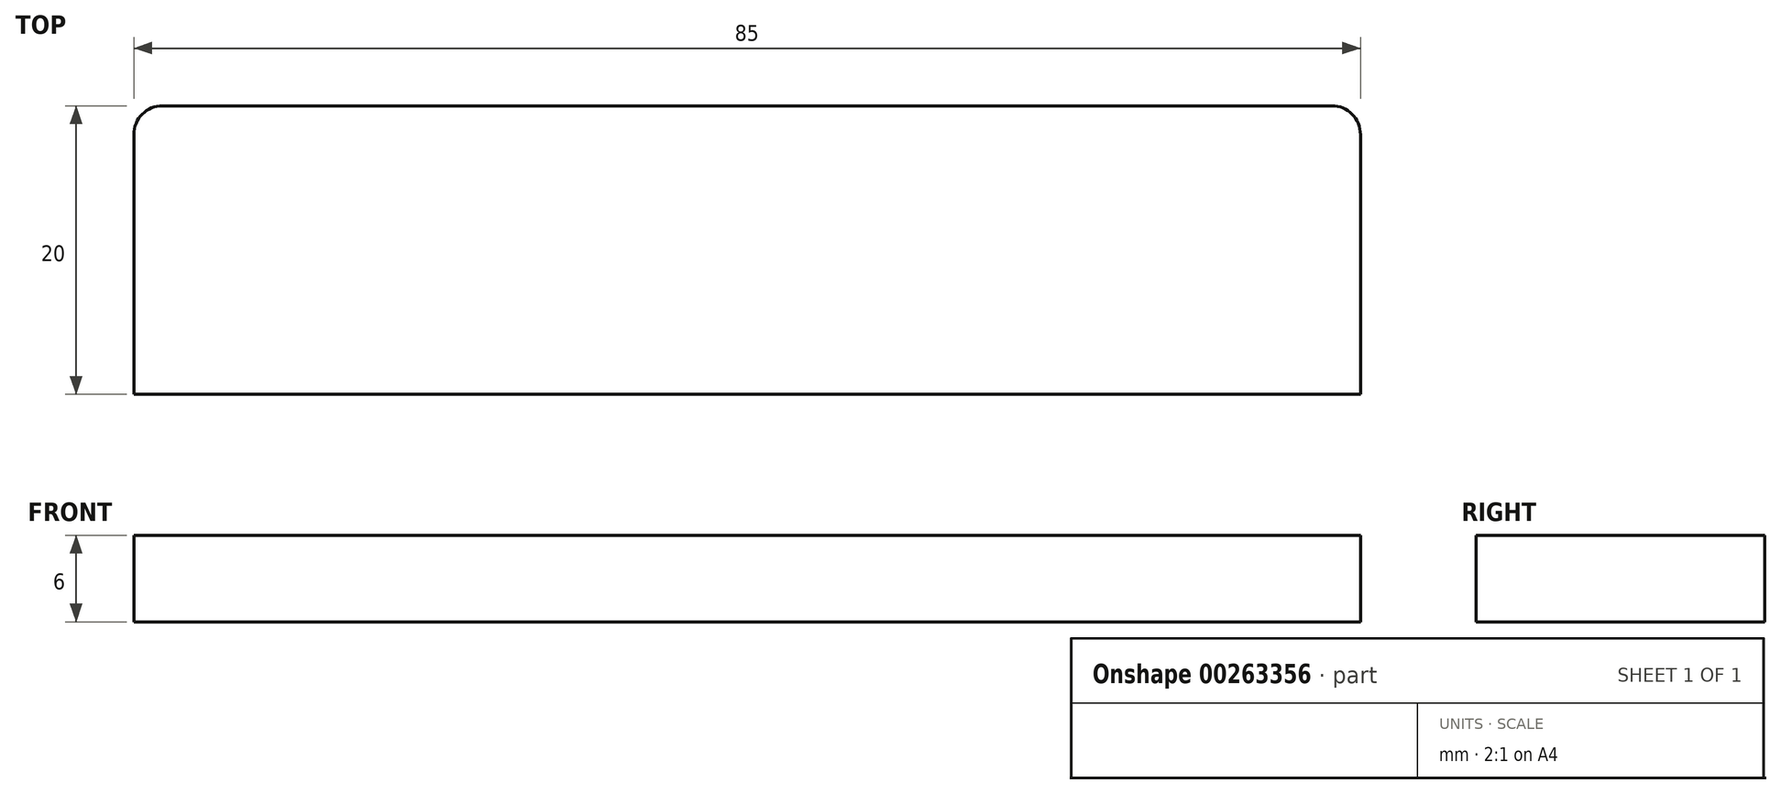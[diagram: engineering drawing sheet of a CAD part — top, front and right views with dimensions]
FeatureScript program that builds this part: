
annotation { "Feature Type Name" : "Feature", "Feature Type Description" : "" }
export const myFeature = defineFeature(function(context is Context, id is Id, definition is map)
    precondition{}
    {
        {
            var Q0;
            Q0=qCreatedBy(makeId("Top.planeOp"),FACE);
            var sketch = newSketch(context, id + "F0", { "sketchPlane" : qUnion([Q0])});
            skLineSegment(sketch, "E0.bottom", {"start": v(0, 0) * mm, "end": v(85, 0) * mm});
            skLineSegment(sketch, "E0.top", {"start": v(2, 20) * mm, "end": v(83, 20) * mm});
            skLineSegment(sketch, "E0.left", {"start": v(0, 0) * mm, "end": v(0, 18) * mm});
            skLineSegment(sketch, "E0.right", {"start": v(85, 0) * mm, "end": v(85, 18) * mm});
            skPoint(sketch, "E1.visualSharp", {"position": v(0, 20) * mm});
            skArc(sketch, "E1.filletArc", {"start": v(2, 20) * mm, "mid": v(0.59, 19.41) * mm, "end": v(0, 18) * mm});
            skPoint(sketch, "E2.visualSharp", {"position": v(85, 20) * mm});
            skArc(sketch, "E2.filletArc", {"start": v(85, 18) * mm, "mid": v(84.41, 19.41) * mm, "end": v(83, 20) * mm});
            skSolve(sketch);
        }
        {
            var Q0;
            Q0 = qSketchRegion(id + "F0", true);
            extrude(context, id + "F1", {"entities" : qUnion([Q0]), "depth" : 6 * mm});
        }
    });
